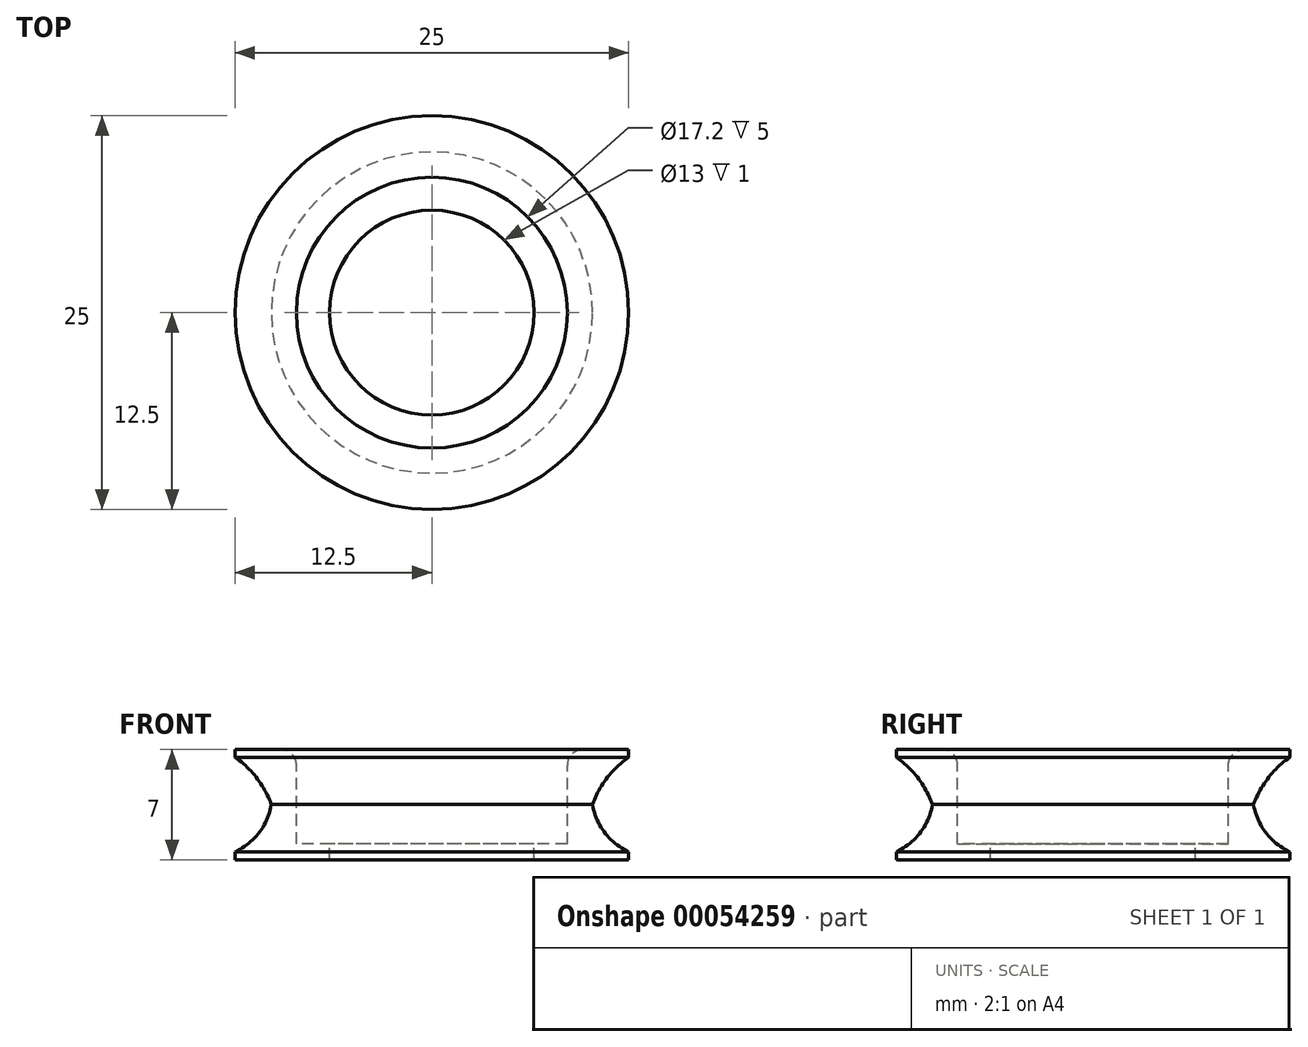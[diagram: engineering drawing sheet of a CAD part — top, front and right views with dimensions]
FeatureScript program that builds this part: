
annotation { "Feature Type Name" : "Feature", "Feature Type Description" : "" }
export const myFeature = defineFeature(function(context is Context, id is Id, definition is map)
    precondition{}
    {
        {
            var Q0;
            Q0=qCreatedBy(makeId("Front.planeOp"),FACE);
            var sketch = newSketch(context, id + "F0", { "sketchPlane" : qUnion([Q0])});
            skLineSegment(sketch, "E0", {"start": v(0, 46.32) * mm, "end": v(0, -24.96) * mm, "construction": true});
            skLineSegment(sketch, "E1.0", {"start": v(-8.6, 46.32) * mm, "end": v(-8.6, -24.96) * mm, "construction": true});
            skLineSegment(sketch, "E2.0", {"start": v(-6.5, 46.32) * mm, "end": v(-6.5, -24.96) * mm, "construction": true});
            skLineSegment(sketch, "E3", {"start": v(-23.38, 0) * mm, "end": v(19.21, 0) * mm, "construction": true});
            skLineSegment(sketch, "E4.0", {"start": v(-12.5, 7) * mm, "end": v(-8.6, 7) * mm, "construction": true});
            skLineSegment(sketch, "E5.0", {"start": v(-10.2, 46.32) * mm, "end": v(-10.2, 8) * mm, "construction": true});
            skLineSegment(sketch, "E6.0", {"start": v(-23.38, 8) * mm, "end": v(19.21, 8) * mm, "construction": true});
            skLineSegment(sketch, "E7.0", {"start": v(-12.5, 1) * mm, "end": v(-10.2, 1) * mm, "construction": true});
            skLineSegment(sketch, "E8.0", {"start": v(-12.5, 46.32) * mm, "end": v(-12.5, 8) * mm, "construction": true});
            skLineSegment(sketch, "E9", {"start": v(-6.5, 1) * mm, "end": v(-8.6, 1) * mm});
            skLineSegment(sketch, "E10", {"start": v(-8.6, 1) * mm, "end": v(-8.6, 7) * mm});
            skLineSegment(sketch, "E11", {"start": v(-8.6, 7) * mm, "end": v(-12.5, 7) * mm});
            skLineSegment(sketch, "E12", {"start": v(-6.5, 1) * mm, "end": v(-6.5, 0) * mm});
            skLineSegment(sketch, "E13", {"start": v(-6.5, 0) * mm, "end": v(-12.5, 0) * mm});
            skLineSegment(sketch, "E14.trimOffspring", {"start": v(-10.2, 0) * mm, "end": v(-10.2, -24.96) * mm, "construction": true});
            skLineSegment(sketch, "E15.trimOffspring", {"start": v(-10.2, 6) * mm, "end": v(-10.2, 1) * mm, "construction": true});
            skLineSegment(sketch, "E16.trimOffspring", {"start": v(-8.6, 1) * mm, "end": v(19.21, 1) * mm, "construction": true});
            skLineSegment(sketch, "E17.trimOffspring", {"start": v(-6.5, 7) * mm, "end": v(19.21, 7) * mm, "construction": true});
            skLineSegment(sketch, "E18.0", {"start": v(-8.6, 6) * mm, "end": v(-12.5, 6) * mm, "construction": true});
            skLineSegment(sketch, "E19.trimOffspring", {"start": v(-12.5, 1) * mm, "end": v(-12.5, 0) * mm, "construction": true});
            skLineSegment(sketch, "E20.trimOffspring", {"start": v(-12.5, 7) * mm, "end": v(-12.5, 6) * mm, "construction": true});
            skArc(sketch, "E21", {"start": v(-10.2, 3.5) * mm, "mid": v(-11.11, 5.18) * mm, "end": v(-12.5, 6.5) * mm});
            skArc(sketch, "E22", {"start": v(-12.5, 0.5) * mm, "mid": v(-10.98, 1.71) * mm, "end": v(-10.2, 3.5) * mm});
            skLineSegment(sketch, "E23", {"start": v(-12.5, 7) * mm, "end": v(-12.5, 6.5) * mm});
            skLineSegment(sketch, "E24", {"start": v(-12.5, 0.5) * mm, "end": v(-12.5, 0) * mm});
            skSolve(sketch);
        }
        {
            var Q0;
            Q0=makeQuery(id+"F0.imprint","IMPRINT",FACE,{"disambiguationData":[TD([[makeQuery(id+"F0.imprint","IMPRINT",EDGE,{"derivedFrom":sQuery(id+"F0.wireOp",EDGE,"E9")}),1.0]])]});
            var Q1;
            Q1=sQuery(id+"F0.wireOp",EDGE,"E0");
            revolve(context, id + "F1", {"entities" : qUnion([Q0]), "axis" : qUnion([Q1]), "revolveType" : RevolveType.FULL});
        }
        {
            var Q0;
            Q0=makeQuery(id+"F1.opRevolve","SWEPT_EDGE",EDGE,{"disambiguationData":[OSD([sQuery(id+"F0.wireOp",EDGE,"E10"),sQuery(id+"F0.wireOp",EDGE,"E11")])]});
            fillet(context, id + "F2", {"entities" : qUnion([Q0]), "radius" : 1 * mm, "tangentPropagation" : true, "allowEdgeOverflow" : false});
        }
    });
